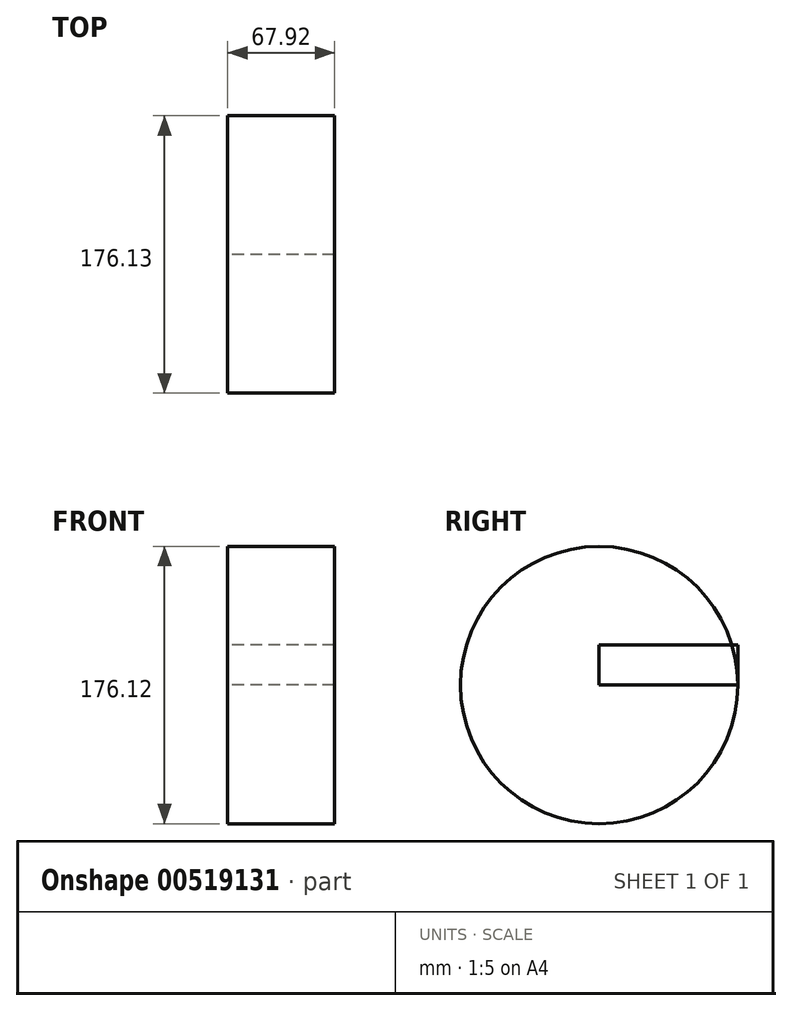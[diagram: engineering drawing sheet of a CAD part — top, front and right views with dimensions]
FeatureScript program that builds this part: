
annotation { "Feature Type Name" : "Feature", "Feature Type Description" : "" }
export const myFeature = defineFeature(function(context is Context, id is Id, definition is map)
    precondition{}
    {
        {
            var Q0;
            Q0=qCreatedBy(makeId("Top.planeOp"),FACE);
            var sketch = newSketch(context, id + "F0", { "sketchPlane" : qUnion([Q0])});
            skLineSegment(sketch, "E0.bottom", {"start": v(33.96, 44.03) * mm, "end": v(-33.96, 44.03) * mm});
            skLineSegment(sketch, "E0.top", {"start": v(33.96, -44.03) * mm, "end": v(-33.96, -44.03) * mm});
            skLineSegment(sketch, "E0.left", {"start": v(33.96, 44.03) * mm, "end": v(33.96, -44.03) * mm});
            skLineSegment(sketch, "E0.right", {"start": v(-33.96, 44.03) * mm, "end": v(-33.96, -44.03) * mm});
            skPoint(sketch, "E0.middle", {"position": v(0, 0) * mm});
            skSolve(sketch);
        }
        {
            var Q0;
            Q0=makeQuery(id+"F0.imprint","IMPRINT",FACE,{"disambiguationData":[TD([[makeQuery(id+"F0.imprint","IMPRINT",EDGE,{"derivedFrom":sQuery(id+"F0.wireOp",EDGE,"E0.bottom")}),1.0]])]});
            var Q1;
            Q1=sQuery(id+"F0.wireOp",EDGE,"E0.top");
            revolve(context, id + "F1", {"entities" : qUnion([Q0]), "axis" : qUnion([Q1]), "revolveType" : RevolveType.FULL});
        }
        {
            var Q0;
            Q0=makeQuery(id+"F0.imprint","IMPRINT",FACE,{"disambiguationData":[TD([[makeQuery(id+"F0.imprint","IMPRINT",EDGE,{"derivedFrom":sQuery(id+"F0.wireOp",EDGE,"E0.bottom")}),1.0]])]});
            extrude(context, id + "F2", {"entities" : qUnion([Q0]), "depth" : 25.4 * mm});
        }
    });
